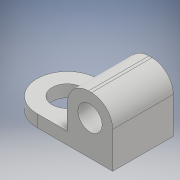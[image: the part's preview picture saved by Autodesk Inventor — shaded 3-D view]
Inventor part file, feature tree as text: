
AUTODESK INVENTOR PART (.ipt)
format: ipt  version: 2017 (Build 210142000, 142)  size: 125,440 bytes
history: native  units: mm
features: extrude x2, sketch x2, fillet x1
ambient origin geometry x8: Origin, YZ Plane, XZ Plane, XY Plane, X Axis, Y Axis, Z Axis, Center Point
bodies: Solid1 (feature_tree)
feature tree (5):
  extrude  "Extrusion1"  Depth=5.0mm
  extrude  "Extrusion2"  Depth=4.0mm TaperAngle=0.0deg
  fillet  "Fillet1"  Radius=8.0mm
  sketch  "Sketch1"  dims[d0=10.0mm d1=5.0mm]
  sketch  "Sketch2"  dims[d2=25.0mm d3=4.0mm d4=0.0mm d5=8.0mm d6=15.0mm d7=15.0mm d8=4.0mm d9=0.0mm d10=7.0mm]
